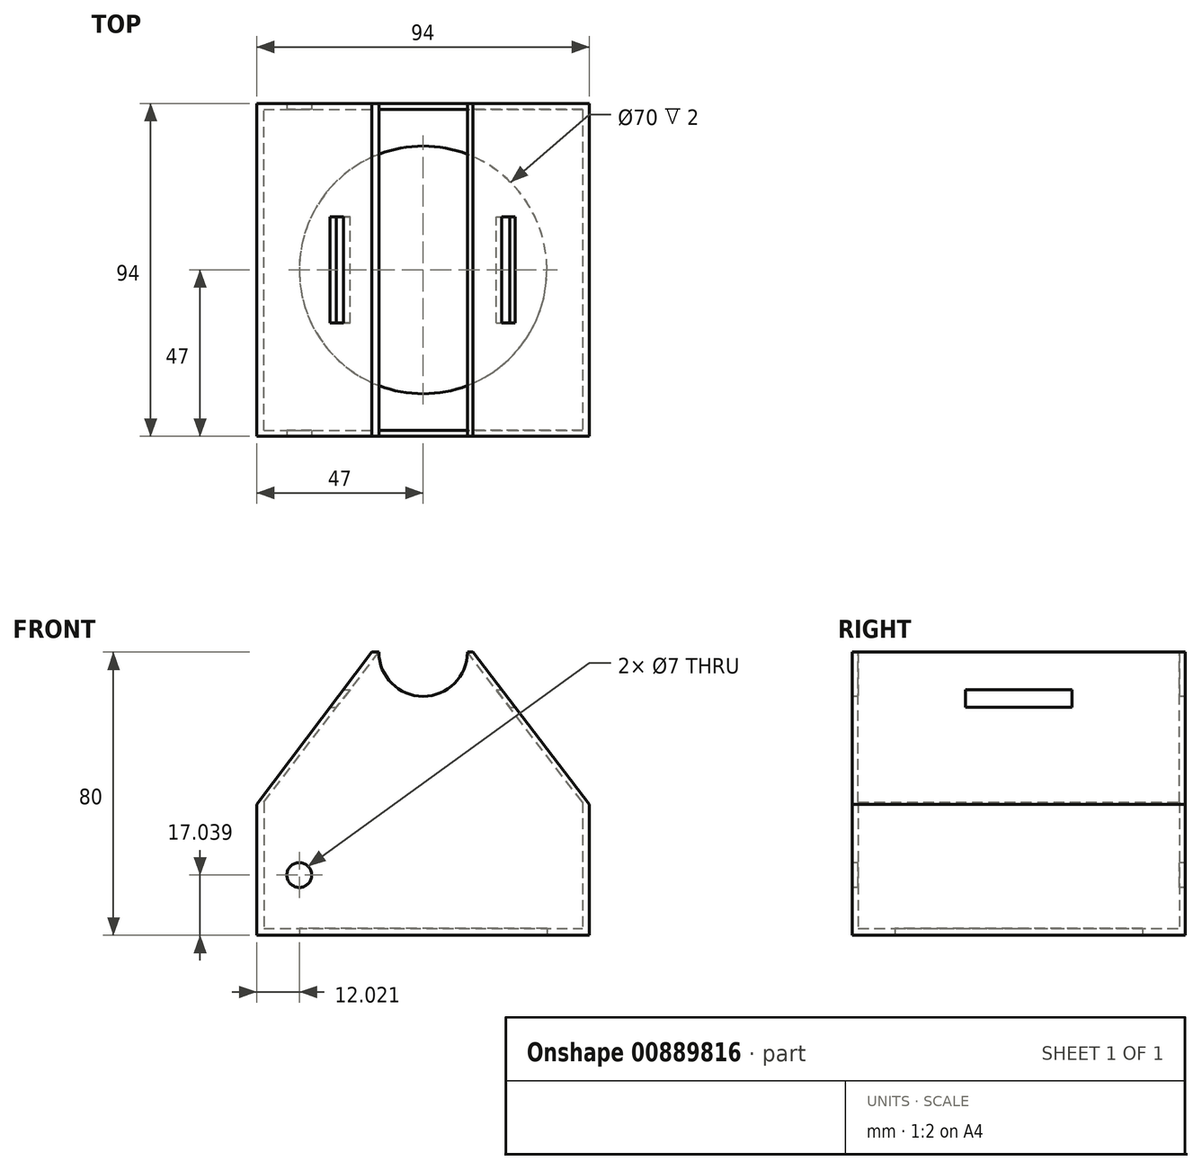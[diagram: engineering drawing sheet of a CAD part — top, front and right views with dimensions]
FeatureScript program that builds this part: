
annotation { "Feature Type Name" : "Feature", "Feature Type Description" : "" }
export const myFeature = defineFeature(function(context is Context, id is Id, definition is map)
    precondition{}
    {
        {
            var Q0;
            Q0=qCreatedBy(makeId("Top.planeOp"),FACE);
            var sketch = newSketch(context, id + "F0", { "sketchPlane" : qUnion([Q0])});
            skCircle(sketch, "E0", {"center": v(0, 0) * mm, "radius": 35 * mm});
            skLineSegment(sketch, "E1.bottom", {"start": v(45, 45.38) * mm, "end": v(-45, 45.38) * mm});
            skLineSegment(sketch, "E1.top", {"start": v(45, -45.38) * mm, "end": v(-45, -45.38) * mm});
            skLineSegment(sketch, "E1.left", {"start": v(45, 45.38) * mm, "end": v(45, -45.38) * mm});
            skLineSegment(sketch, "E1.right", {"start": v(-45, 45.38) * mm, "end": v(-45, -45.38) * mm});
            skLineSegment(sketch, "E2.bottom", {"start": v(47, 47) * mm, "end": v(-47, 47) * mm});
            skLineSegment(sketch, "E2.top", {"start": v(47, -47) * mm, "end": v(-47, -47) * mm});
            skLineSegment(sketch, "E2.left", {"start": v(47, 47) * mm, "end": v(47, -47) * mm});
            skLineSegment(sketch, "E2.right", {"start": v(-47, 47) * mm, "end": v(-47, -47) * mm});
            skSolve(sketch);
        }
        {
            var Q0;
            Q0 = qSketchRegion(id + "F0", true);
            var Q1;
            Q1=makeQuery(id+"F0.imprint","IMPRINT",FACE,{"disambiguationData":[TD([[makeQuery(id+"F0.imprint","IMPRINT",EDGE,{"derivedFrom":sQuery(id+"F0.wireOp",EDGE,"E0")}),-1.0]])]});
            extrude(context, id + "F1", {"entities" : qUnion([Q0, Q1]), "depth" : 2 * mm, "offsetDistance" : 25 * mm});
        }
        {
            var Q0;
            Q0=makeQuery(id+"F0.imprint","IMPRINT",FACE,{"disambiguationData":[TD([[makeQuery(id+"F0.imprint","IMPRINT",EDGE,{"derivedFrom":sQuery(id+"F0.wireOp",EDGE,"E1.bottom")}),-1.0]])]});
            extrude(context, id + "F2", {"entities" : qUnion([Q0]), "operationType" : NewBodyOperationType.ADD, "depth" : 80 * mm, "offsetDistance" : 25 * mm});
        }
        {
            var Q0;
            {var subQ0=sQuery(id+"F0.wireOp",EDGE,"E2.top");Q0=makeQuery(id+"F2.boolean.opBoolean","MERGE",FACE,{"derivedFrom":[makeQuery(id+"F1.opExtrude","SWEPT_FACE",FACE,{"disambiguationData":[OSD([subQ0])]}),makeQuery(id+"F2.opExtrude","SWEPT_FACE",FACE,{"disambiguationData":[OSD([subQ0])]})]});}
            var sketch = newSketch(context, id + "F3", { "sketchPlane" : qUnion([Q0])});
            skCircle(sketch, "E3", {"center": v(0, 80) * mm, "radius": 12.5 * mm});
            skCircle(sketch, "E4", {"center": v(-34.98, 17.04) * mm, "radius": 3.5 * mm});
            skLineSegment(sketch, "E5", {"start": v(-47, 0) * mm, "end": v(-47, 35) * mm});
            skLineSegment(sketch, "E6", {"start": v(-47, 35) * mm, "end": v(-12.5, 80) * mm});
            skLineSegment(sketch, "E7", {"start": v(47, 0) * mm, "end": v(47, 35) * mm});
            skLineSegment(sketch, "E8", {"start": v(47, 35) * mm, "end": v(12.5, 80) * mm});
            skLineSegment(sketch, "E9", {"start": v(-12.5, 80) * mm, "end": v(-14.5, 80) * mm});
            skLineSegment(sketch, "E10", {"start": v(-14.5, 80) * mm, "end": v(-47, 37) * mm});
            skLineSegment(sketch, "E11", {"start": v(-47, 37) * mm, "end": v(-47, 35) * mm});
            skLineSegment(sketch, "E12", {"start": v(12.5, 80) * mm, "end": v(14.03, 80) * mm});
            skLineSegment(sketch, "E13", {"start": v(14.03, 80) * mm, "end": v(47, 37) * mm});
            skPoint(sketch, "E13.endSnap0", {"position": v(47, 40) * mm});
            skLineSegment(sketch, "E14", {"start": v(47, 37) * mm, "end": v(47, 35) * mm});
            skLineSegment(sketch, "E15", {"start": v(47, 37) * mm, "end": v(47, 80) * mm});
            skLineSegment(sketch, "E16", {"start": v(47, 80) * mm, "end": v(14.03, 80) * mm});
            skLineSegment(sketch, "E17", {"start": v(-14.5, 80) * mm, "end": v(-47, 80) * mm});
            skLineSegment(sketch, "E18", {"start": v(-47, 80) * mm, "end": v(-47, 37) * mm});
            skSolve(sketch);
        }
        {
            var Q0;
            {var subQ0=sQuery(id+"F3.wireOp",EDGE,"E3");var subQ1=makeQuery(id+"F2.opExtrude","CAP_EDGE",EDGE,{"disambiguationData":[OSD([sQuery(id+"F0.wireOp",EDGE,"E2.top")])],"isStart":false});var subQ2=makeQuery(id+"F3.imprint","INTERSECT",VERTEX,{"disambiguationData":[OD(0.0)],"derivedFrom":[subQ1,subQ0]});Q0=makeQuery(id+"F3.imprint","IMPRINT",FACE,{"disambiguationData":[TD([[makeQuery(id+"F3.imprint","IMPRINT",EDGE,{"disambiguationData":[TD([[subQ2,1.0]])],"derivedFrom":subQ0}),1.0]])]});}
            var Q1;
            Q1=makeQuery(id+"F3.imprint","IMPRINT",FACE,{"disambiguationData":[TD([[makeQuery(id+"F3.imprint","IMPRINT",EDGE,{"derivedFrom":sQuery(id+"F3.wireOp",EDGE,"E4")}),1.0]])]});
            extrude(context, id + "F4", {"entities" : qUnion([Q0, Q1]), "operationType" : NewBodyOperationType.REMOVE, "oppositeDirection" : true, "depth" : 100 * mm, "offsetDistance" : 25 * mm});
        }
        {
            var Q0;
            {var subQ0=sQuery(id+"F3.wireOp",EDGE,"E10");Q0=makeQuery(id+"F3.imprint","IMPRINT",FACE,{"disambiguationData":[TD([[makeQuery(id+"F3.imprint","IMPRINT",EDGE,{"derivedFrom":subQ0}),-1.0]])]});}
            var Q1;
            Q1=makeQuery(id+"F3.imprint","IMPRINT",FACE,{"disambiguationData":[TD([[makeQuery(id+"F3.imprint","IMPRINT",EDGE,{"derivedFrom":sQuery(id+"F3.wireOp",EDGE,"E13")}),1.0]])]});
            extrude(context, id + "F5", {"entities" : qUnion([Q0, Q1]), "operationType" : NewBodyOperationType.REMOVE, "oppositeDirection" : true, "depth" : 150 * mm, "offsetDistance" : 25 * mm});
        }
        {
            var Q0;
            Q0=makeQuery(id+"F3.imprint","IMPRINT",FACE,{"disambiguationData":[TD([[makeQuery(id+"F3.imprint","IMPRINT",EDGE,{"derivedFrom":sQuery(id+"F3.wireOp",EDGE,"E6")}),1.0]])]});
            var Q1;
            Q1=makeQuery(id+"F3.imprint","IMPRINT",FACE,{"disambiguationData":[TD([[makeQuery(id+"F3.imprint","IMPRINT",EDGE,{"derivedFrom":sQuery(id+"F3.wireOp",EDGE,"E8")}),-1.0]])]});
            extrude(context, id + "F6", {"entities" : qUnion([Q0, Q1]), "operationType" : NewBodyOperationType.ADD, "depth" : -94 * mm, "offsetDistance" : 25 * mm});
        }
        {
            var Q0;
            {var subQ0=sQuery(id+"F0.wireOp",EDGE,"E2.left");Q0=makeQuery(id+"F2.boolean.opBoolean","MERGE",FACE,{"derivedFrom":[makeQuery(id+"F1.opExtrude","SWEPT_FACE",FACE,{"disambiguationData":[OSD([subQ0])]}),makeQuery(id+"F2.opExtrude","SWEPT_FACE",FACE,{"disambiguationData":[OSD([subQ0])]})]});}
            var sketch = newSketch(context, id + "F7", { "sketchPlane" : qUnion([Q0])});
            skLineSegment(sketch, "E19.bottom", {"start": v(-15, 69.38) * mm, "end": v(15, 69.38) * mm});
            skLineSegment(sketch, "E19.top", {"start": v(-15, 64.38) * mm, "end": v(15, 64.38) * mm});
            skLineSegment(sketch, "E19.left", {"start": v(-15, 69.38) * mm, "end": v(-15, 64.38) * mm});
            skLineSegment(sketch, "E19.right", {"start": v(15, 69.38) * mm, "end": v(15, 64.38) * mm});
            skSolve(sketch);
        }
        {
            var Q0;
            Q0=makeQuery(id+"F7.imprint","IMPRINT",FACE,{"disambiguationData":[TD([[makeQuery(id+"F7.imprint","IMPRINT",EDGE,{"derivedFrom":sQuery(id+"F7.wireOp",EDGE,"E19.bottom")}),-1.0]])]});
            extrude(context, id + "F8", {"entities" : qUnion([Q0]), "operationType" : NewBodyOperationType.REMOVE, "oppositeDirection" : true, "depth" : 100 * mm, "offsetDistance" : 25 * mm});
        }
    });
